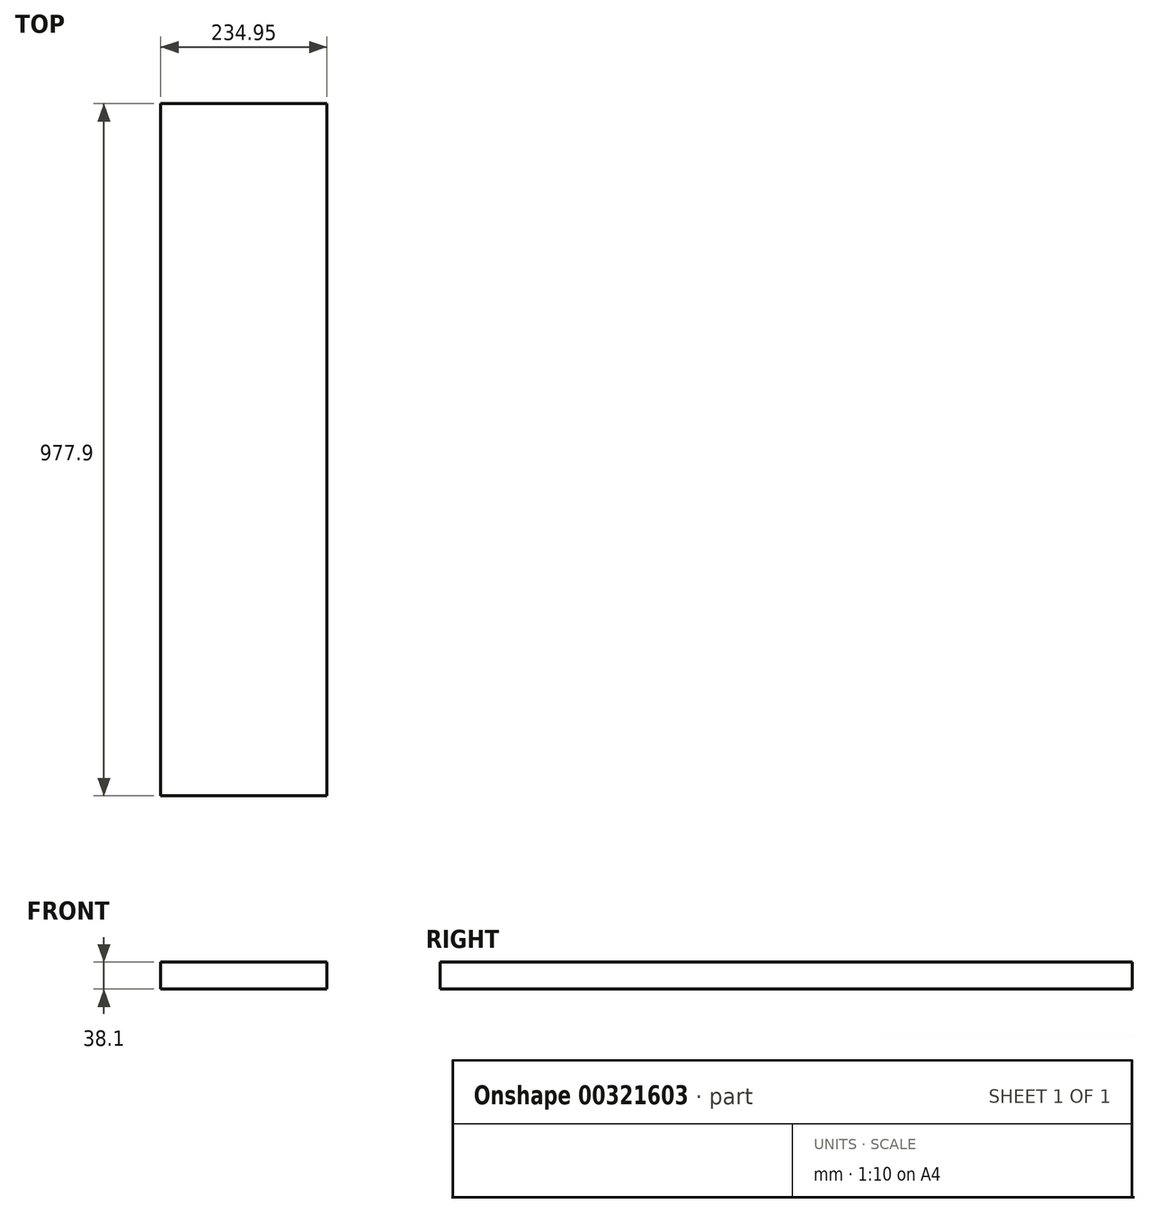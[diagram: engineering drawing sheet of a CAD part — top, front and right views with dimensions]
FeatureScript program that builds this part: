
annotation { "Feature Type Name" : "Feature", "Feature Type Description" : "" }
export const myFeature = defineFeature(function(context is Context, id is Id, definition is map)
    precondition{}
    {
        {
            var Q0;
            Q0=qCreatedBy(makeId("Front.planeOp"),FACE);
            var sketch = newSketch(context, id + "F0", { "sketchPlane" : qUnion([Q0])});
            skLineSegment(sketch, "E0.bottom", {"start": v(-104.84, 11.33) * mm, "end": v(130.1, 11.33) * mm});
            skLineSegment(sketch, "E0.top", {"start": v(-104.84, -26.77) * mm, "end": v(130.1, -26.77) * mm});
            skLineSegment(sketch, "E0.left", {"start": v(-104.84, 11.33) * mm, "end": v(-104.84, -26.77) * mm});
            skLineSegment(sketch, "E0.right", {"start": v(130.1, 11.33) * mm, "end": v(130.1, -26.77) * mm});
            skSolve(sketch);
        }
        {
            var Q0;
            Q0=makeQuery(id+"F0.imprint","IMPRINT",FACE,{"disambiguationData":[TD([[makeQuery(id+"F0.imprint","IMPRINT",EDGE,{"derivedFrom":sQuery(id+"F0.wireOp",EDGE,"E0.bottom")}),-1.0]])]});
            extrude(context, id + "F1", {"entities" : qUnion([Q0]), "depth" : 977.9 * mm});
        }
    });
